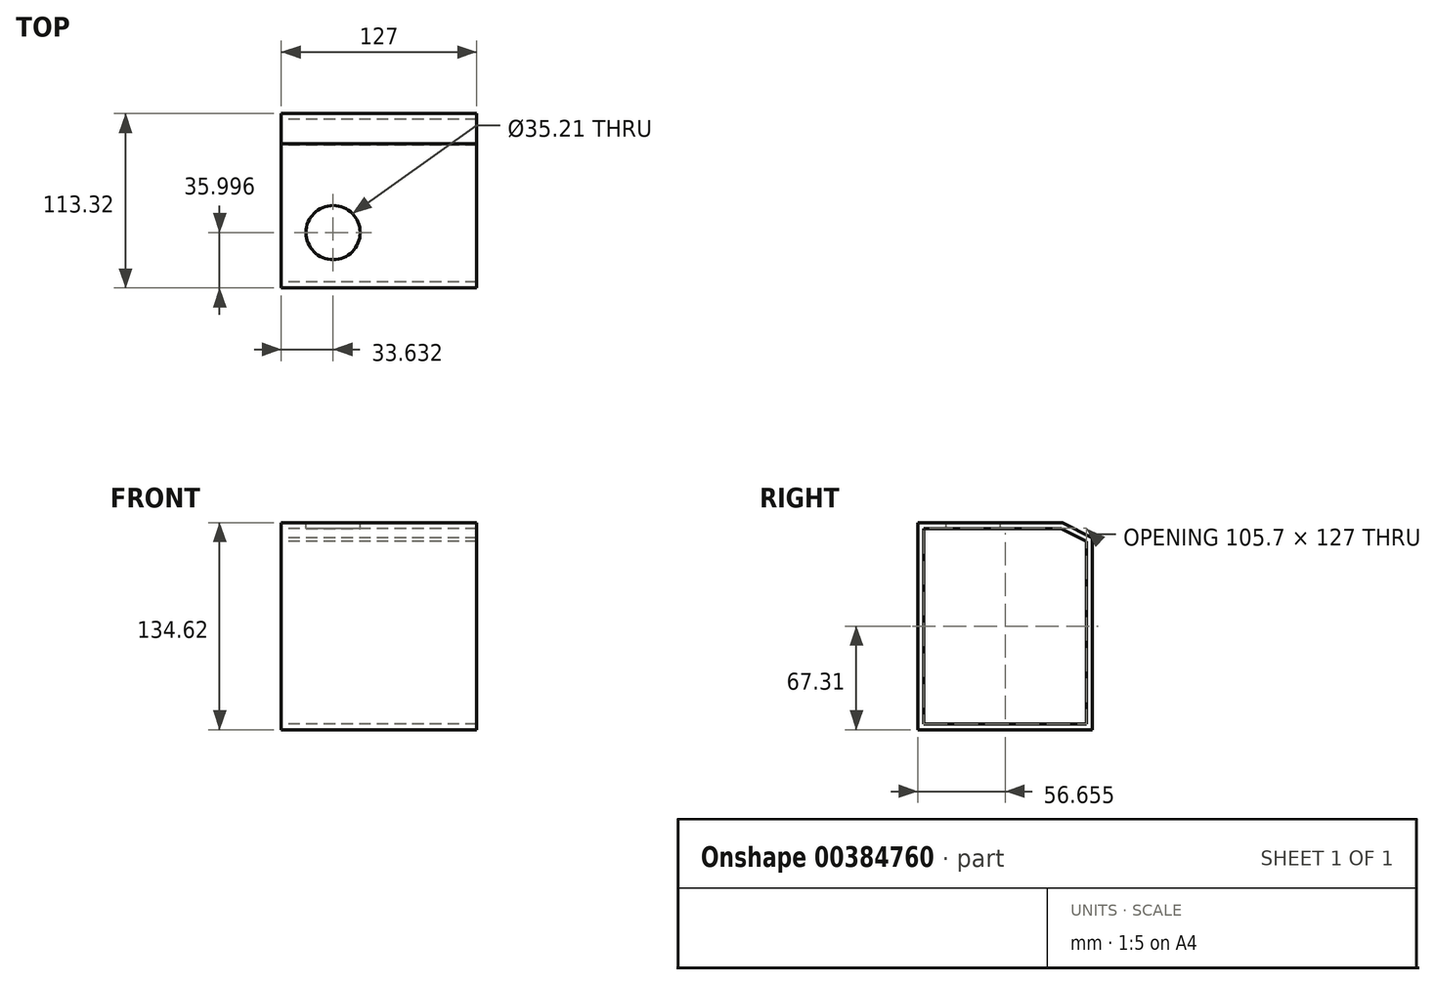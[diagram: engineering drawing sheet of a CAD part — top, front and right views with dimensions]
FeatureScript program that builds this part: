
annotation { "Feature Type Name" : "Feature", "Feature Type Description" : "" }
export const myFeature = defineFeature(function(context is Context, id is Id, definition is map)
    precondition{}
    {
        {
            var Q0;
            Q0=qCreatedBy(makeId("Right.planeOp"),FACE);
            var sketch = newSketch(context, id + "F0", { "sketchPlane" : qUnion([Q0])});
            skLineSegment(sketch, "E0", {"start": v(-57.23, 0) * mm, "end": v(-57.23, 127) * mm});
            skLineSegment(sketch, "E1", {"start": v(-57.23, 127) * mm, "end": v(31.82, 127) * mm});
            skLineSegment(sketch, "E2", {"start": v(31.82, 127) * mm, "end": v(48.47, 118.5) * mm});
            skLineSegment(sketch, "E3", {"start": v(48.47, 118.5) * mm, "end": v(48.47, 0) * mm});
            skLineSegment(sketch, "E4", {"start": v(48.47, 0) * mm, "end": v(-57.23, 0) * mm});
            skLineSegment(sketch, "E5.0", {"start": v(32.73, 130.8) * mm, "end": v(52.28, 120.82) * mm});
            skLineSegment(sketch, "E5.1", {"start": v(-61.04, 130.8) * mm, "end": v(32.73, 130.8) * mm});
            skLineSegment(sketch, "E5.2", {"start": v(52.28, 120.82) * mm, "end": v(52.28, -3.81) * mm});
            skLineSegment(sketch, "E5.3", {"start": v(52.28, -3.81) * mm, "end": v(-61.04, -3.81) * mm});
            skLineSegment(sketch, "E5.4", {"start": v(-61.04, -3.81) * mm, "end": v(-61.04, 130.8) * mm});
            skSolve(sketch);
        }
        {
            var Q0;
            Q0 = qSketchRegion(id + "F0", true);
            extrude(context, id + "F1", {"entities" : qUnion([Q0]), "endBound" : BoundingType.SYMMETRIC, "depth" : 127 * mm});
        }
        {
            var Q0;
            Q0=makeQuery(id+"F1.opExtrude","SWEPT_FACE",FACE,{"disambiguationData":[OSD([sQuery(id+"F0.wireOp",EDGE,"E5.1")])]});
            var sketch = newSketch(context, id + "F2", { "sketchPlane" : qUnion([Q0])});
            skCircle(sketch, "E6", {"center": v(-29.87, -25.04) * mm, "radius": 17.6 * mm});
            skCircle(sketch, "E7.0", {"center": v(-29.87, -25.04) * mm, "radius": 20.15 * mm});
            skLineSegment(sketch, "E8.0", {"start": v(-57.15, 26.38) * mm, "end": v(-57.15, -54.7) * mm});
            skLineSegment(sketch, "E8.1", {"start": v(57.15, 26.38) * mm, "end": v(-57.15, 26.38) * mm});
            skLineSegment(sketch, "E8.2", {"start": v(57.15, -54.7) * mm, "end": v(57.15, 26.38) * mm});
            skLineSegment(sketch, "E8.3", {"start": v(-57.15, -54.7) * mm, "end": v(57.15, -54.7) * mm});
            skSolve(sketch);
        }
        {
            var Q0;
            Q0=makeQuery(id+"F2.imprint","IMPRINT",FACE,{"disambiguationData":[TD([[makeQuery(id+"F2.imprint","IMPRINT",EDGE,{"derivedFrom":sQuery(id+"F2.wireOp",EDGE,"E6")}),1.0]])]});
            extrude(context, id + "F3", {"entities" : qUnion([Q0]), "operationType" : NewBodyOperationType.REMOVE, "endBound" : BoundingType.UP_TO_NEXT, "oppositeDirection" : true, "depth" : 25.4 * mm});
        }
    });
